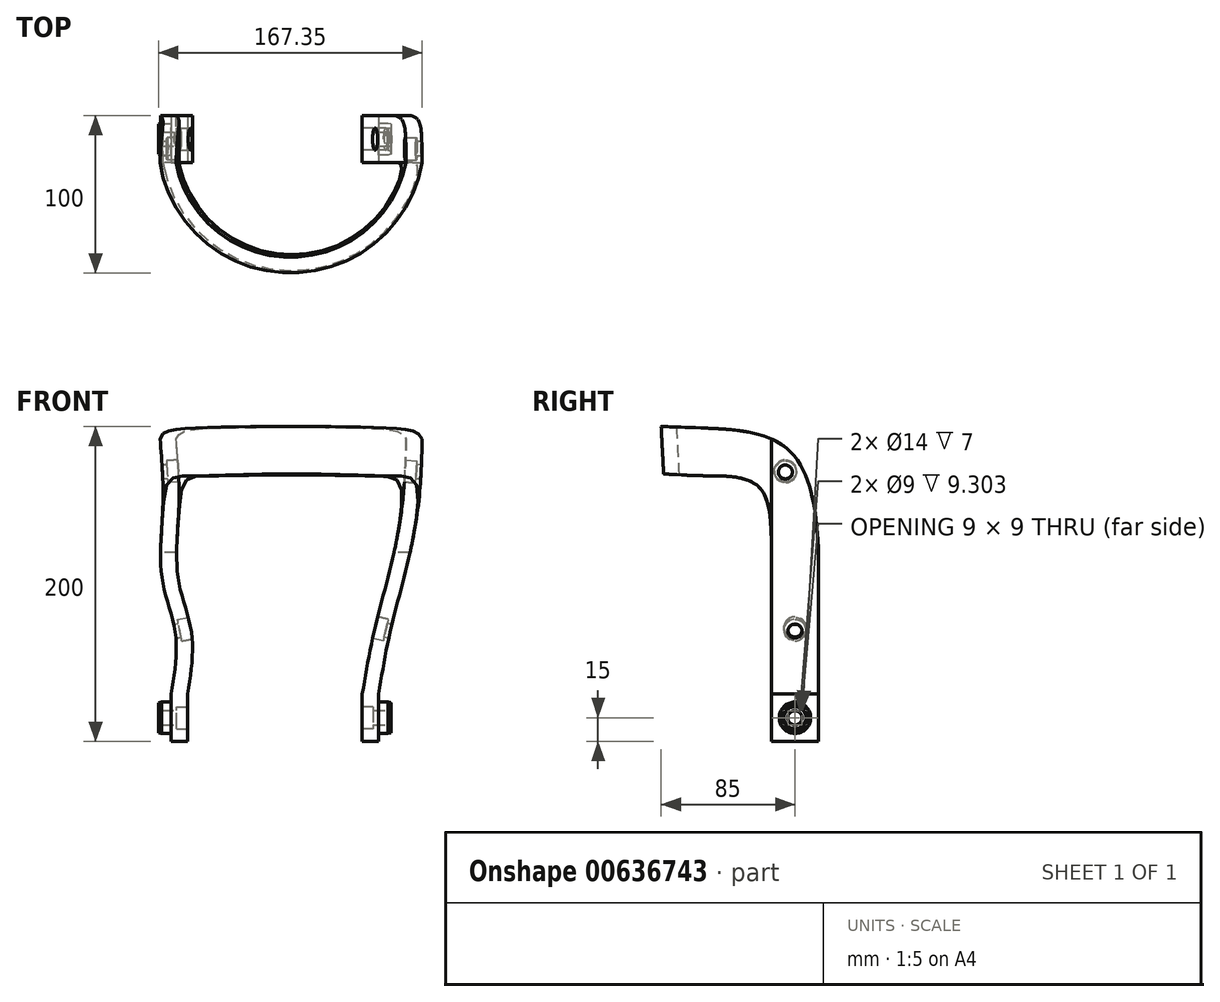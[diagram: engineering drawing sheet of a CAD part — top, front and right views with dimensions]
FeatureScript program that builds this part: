
annotation { "Feature Type Name" : "Feature", "Feature Type Description" : "" }
export const myFeature = defineFeature(function(context is Context, id is Id, definition is map)
    precondition{}
    {
        {
            var Q0;
            Q0=qCreatedBy(makeId("Top.planeOp"),FACE);
            var sketch = newSketch(context, id + "F0", { "sketchPlane" : qUnion([Q0])});
            skLineSegment(sketch, "E0", {"start": v(-55.5, 15) * mm, "end": v(-55.5, -15) * mm});
            skLineSegment(sketch, "E1", {"start": v(55.5, 15) * mm, "end": v(55.5, -15) * mm});
            skPoint(sketch, "E2", {"position": v(-55.5, 0) * mm});
            skPoint(sketch, "E3", {"position": v(55.5, 0) * mm});
            skLineSegment(sketch, "E4", {"start": v(-55.5, 15) * mm, "end": v(-65.81, 15) * mm});
            skLineSegment(sketch, "E5", {"start": v(-65.81, 15) * mm, "end": v(-65.81, -15) * mm});
            skLineSegment(sketch, "E6", {"start": v(55.5, 15) * mm, "end": v(65.81, 15) * mm});
            skLineSegment(sketch, "E7", {"start": v(65.81, 15) * mm, "end": v(65.81, -15) * mm});
            skLineSegment(sketch, "E8", {"start": v(-65.81, -15) * mm, "end": v(-55.5, -15) * mm});
            skLineSegment(sketch, "E9", {"start": v(55.5, -15) * mm, "end": v(65.81, -15) * mm});
            skSolve(sketch);
        }
        {
            var Q0;
            Q0=qCreatedBy(makeId("Top.planeOp"),FACE);
            cPlane(context, id + "F1", {"entities" : qUnion([Q0]), "cplaneType" : CPlaneType.OFFSET, "offset" : 30 * mm, "width" : 150 * mm, "height" : 150 * mm});
        }
        {
            var Q0;
            Q0=qCreatedBy(id+"F1.planeOp",FACE);
            var sketch = newSketch(context, id + "F2", { "sketchPlane" : qUnion([Q0])});
            skArc(sketch, "E10", {"start": v(-55.5, -15) * mm, "mid": v(0, -57.5) * mm, "end": v(55.5, -15) * mm});
            skArc(sketch, "E11", {"start": v(-65.81, -15) * mm, "mid": v(0, -67.5) * mm, "end": v(65.81, -15) * mm});
            skLineSegment(sketch, "E12", {"start": v(-55.5, 15) * mm, "end": v(-55.5, -15) * mm});
            skLineSegment(sketch, "E13", {"start": v(55.5, 15) * mm, "end": v(55.5, -15) * mm});
            skPoint(sketch, "E14", {"position": v(-55.5, 0) * mm});
            skPoint(sketch, "E15", {"position": v(55.5, 0) * mm});
            skLineSegment(sketch, "E16", {"start": v(-55.5, 15) * mm, "end": v(-65.81, 15) * mm});
            skLineSegment(sketch, "E17", {"start": v(-65.81, 15) * mm, "end": v(-65.81, -15) * mm});
            skLineSegment(sketch, "E18", {"start": v(55.5, 15) * mm, "end": v(65.81, 15) * mm});
            skLineSegment(sketch, "E19", {"start": v(65.81, 15) * mm, "end": v(65.81, -15) * mm});
            skSolve(sketch);
        }
        {
            var Q0;
            Q0=qCreatedBy(makeId("Top.planeOp"),FACE);
            cPlane(context, id + "F3", {"entities" : qUnion([Q0]), "cplaneType" : CPlaneType.OFFSET, "offset" : 70 * mm, "width" : 150 * mm, "height" : 150 * mm});
        }
        {
            var Q0;
            Q0=qCreatedBy(id+"F3.planeOp",FACE);
            var sketch = newSketch(context, id + "F4", { "sketchPlane" : qUnion([Q0])});
            skPoint(sketch, "E20", {"position": v(5, 0) * mm});
            skPoint(sketch, "E21.center.orphan", {"position": v(0, 0) * mm});
            skArc(sketch, "E22", {"start": v(-53.1, -15) * mm, "mid": v(5, -60) * mm, "end": v(63.1, -15) * mm});
            skArc(sketch, "E23", {"start": v(-63.37, -15) * mm, "mid": v(5, -70) * mm, "end": v(73.37, -15) * mm});
            skLineSegment(sketch, "E24", {"start": v(-53.1, 15) * mm, "end": v(-53.1, -15) * mm});
            skLineSegment(sketch, "E25", {"start": v(63.1, 15) * mm, "end": v(63.1, -15) * mm});
            skPoint(sketch, "E26", {"position": v(-53.1, 0) * mm});
            skLineSegment(sketch, "E27", {"start": v(-53.1, 15) * mm, "end": v(-63.37, 15) * mm});
            skLineSegment(sketch, "E28", {"start": v(-63.37, 15) * mm, "end": v(-63.37, -15) * mm});
            skLineSegment(sketch, "E29", {"start": v(63.1, 15) * mm, "end": v(73.37, 15) * mm});
            skLineSegment(sketch, "E30", {"start": v(73.37, 15) * mm, "end": v(73.37, -15) * mm});
            skSolve(sketch);
        }
        {
            var Q0;
            Q0=qCreatedBy(makeId("Top.planeOp"),FACE);
            cPlane(context, id + "F5", {"entities" : qUnion([Q0]), "cplaneType" : CPlaneType.OFFSET, "offset" : 100 * mm, "width" : 150 * mm, "height" : 150 * mm});
        }
        {
            var Q0;
            Q0=qCreatedBy(id+"F5.planeOp",FACE);
            var sketch = newSketch(context, id + "F6", { "sketchPlane" : qUnion([Q0])});
            skPoint(sketch, "E31", {"position": v(5, 0) * mm});
            skArc(sketch, "E32", {"start": v(-60.81, -15) * mm, "mid": v(5, -67.5) * mm, "end": v(70.81, -15) * mm});
            skArc(sketch, "E33", {"start": v(-71.03, -15) * mm, "mid": v(5, -77.5) * mm, "end": v(81.03, -15) * mm});
            skLineSegment(sketch, "E34", {"start": v(-60.81, 15) * mm, "end": v(-60.81, -15) * mm});
            skLineSegment(sketch, "E35", {"start": v(70.81, 15) * mm, "end": v(70.81, -15) * mm});
            skLineSegment(sketch, "E36", {"start": v(-60.81, 15) * mm, "end": v(-71.03, 15) * mm});
            skLineSegment(sketch, "E37", {"start": v(-71.03, 15) * mm, "end": v(-71.03, -15) * mm});
            skLineSegment(sketch, "E38", {"start": v(70.81, 15) * mm, "end": v(81.03, 15) * mm});
            skLineSegment(sketch, "E39", {"start": v(81.03, 15) * mm, "end": v(81.03, -15) * mm});
            skSolve(sketch);
        }
        {
            var Q0;
            Q0=qCreatedBy(makeId("Top.planeOp"),FACE);
            cPlane(context, id + "F7", {"entities" : qUnion([Q0]), "cplaneType" : CPlaneType.OFFSET, "offset" : 150 * mm, "width" : 150 * mm, "height" : 150 * mm});
        }
        {
            var Q0;
            Q0=qCreatedBy(id+"F7.planeOp",FACE);
            var sketch = newSketch(context, id + "F8", { "sketchPlane" : qUnion([Q0])});
            skPoint(sketch, "E40", {"position": v(10, 0) * mm});
            skArc(sketch, "E41", {"start": v(-60.93, -15) * mm, "mid": v(10, -72.5) * mm, "end": v(80.93, -15) * mm});
            skArc(sketch, "E42", {"start": v(-71.12, -15) * mm, "mid": v(10, -82.5) * mm, "end": v(91.12, -15) * mm});
            skLineSegment(sketch, "E43", {"start": v(-60.93, 15) * mm, "end": v(-60.93, -15) * mm});
            skLineSegment(sketch, "E44", {"start": v(80.93, -15) * mm, "end": v(80.93, 15) * mm});
            skPoint(sketch, "E45", {"position": v(-60.93, 0) * mm});
            skPoint(sketch, "E46", {"position": v(80.93, 0) * mm});
            skLineSegment(sketch, "E47", {"start": v(-60.93, 15) * mm, "end": v(-71.12, 15) * mm});
            skLineSegment(sketch, "E48", {"start": v(-71.12, 15) * mm, "end": v(-71.12, -15) * mm});
            skLineSegment(sketch, "E49", {"start": v(80.93, 15) * mm, "end": v(91.12, 15) * mm});
            skLineSegment(sketch, "E50", {"start": v(91.12, 15) * mm, "end": v(91.12, -15) * mm});
            skSolve(sketch);
        }
        {
            var Q0;
            Q0=qCreatedBy(makeId("Top.planeOp"),FACE);
            cPlane(context, id + "F9", {"entities" : qUnion([Q0]), "cplaneType" : CPlaneType.OFFSET, "offset" : 200 * mm, "width" : 150 * mm, "height" : 150 * mm});
        }
        {
            var Q0;
            Q0=qCreatedBy(id+"F9.planeOp",FACE);
            var sketch = newSketch(context, id + "F10", { "sketchPlane" : qUnion([Q0])});
            skPoint(sketch, "E51", {"position": v(10, 0) * mm});
            skArc(sketch, "E52", {"start": v(-63.48, -15) * mm, "mid": v(10, -75) * mm, "end": v(83.48, -15) * mm});
            skArc(sketch, "E53", {"start": v(-73.67, -15) * mm, "mid": v(10, -85) * mm, "end": v(93.67, -15) * mm});
            skLineSegment(sketch, "E54", {"start": v(-63.48, 15) * mm, "end": v(-63.48, -15) * mm});
            skLineSegment(sketch, "E55", {"start": v(83.48, 15) * mm, "end": v(83.48, -15) * mm});
            skLineSegment(sketch, "E56", {"start": v(-63.48, 15) * mm, "end": v(-73.67, 15) * mm});
            skLineSegment(sketch, "E57", {"start": v(-73.67, 15) * mm, "end": v(-73.67, -15) * mm});
            skLineSegment(sketch, "E58", {"start": v(83.48, 15) * mm, "end": v(93.67, 15) * mm});
            skLineSegment(sketch, "E59", {"start": v(93.67, 15) * mm, "end": v(93.67, -15) * mm});
            skSolve(sketch);
        }
        {
            var Q0;
            Q0=qSketchRegion(id+"F2",true);
            var Q1;
            Q1=qSketchRegion(id+"F4",true);
            var Q2;
            Q2=qSketchRegion(id+"F6",true);
            var Q3;
            Q3=qSketchRegion(id+"F8",true);
            var Q4;
            Q4=qSketchRegion(id+"F10",true);
            loft(context, id + "F11", {"sheetProfilesArray" : [{ "sheetProfileEntities" : qUnion([Q0]) }, { "sheetProfileEntities" : qUnion([Q1]) }, { "sheetProfileEntities" : qUnion([Q2]) }, { "sheetProfileEntities" : qUnion([Q3]) }, { "sheetProfileEntities" : qUnion([Q4]) }]});
        }
        {
            var Q0;
            Q0=qCreatedBy(makeId("Right.planeOp"),FACE);
            cPlane(context, id + "F12", {"entities" : qUnion([Q0]), "cplaneType" : CPlaneType.OFFSET, "offset" : 77 * mm, "oppositeDirection" : true, "width" : 150 * mm, "height" : 150 * mm});
        }
        {
            var Q0;
            Q0=qCreatedBy(id+"F12.planeOp",FACE);
            var sketch = newSketch(context, id + "F13", { "sketchPlane" : qUnion([Q0])});
            skPoint(sketch, "E60", {"position": v(-85, 200) * mm});
            skLineSegment(sketch, "E61", {"start": v(-85, 200) * mm, "end": v(-85, 170) * mm});
            skPoint(sketch, "E62", {"position": v(15, 200) * mm});
            skLineSegment(sketch, "E63", {"start": v(15, 200) * mm, "end": v(15, 120) * mm});
            skPoint(sketch, "E64", {"position": v(15, 0) * mm});
            skPoint(sketch, "E65", {"position": v(-15, 0) * mm});
            skPoint(sketch, "E66", {"position": v(-15, 200) * mm});
            skFitSpline(sketch, "E67", {"points": [v(-85, 200) * mm, v(15, 120) * mm], "startDerivative": vector(199.24, -8.69) * mm, "endDerivative": vector(9.95, -251.27) * mm});
            skPoint(sketch, "E68", {"position": v(-56.51, 168.7) * mm});
            skPoint(sketch, "E69", {"position": v(-23.21, 161.98) * mm});
            skPoint(sketch, "E70", {"position": v(-50.86, 198.7) * mm});
            skPoint(sketch, "E71", {"position": v(-4.39, 185.34) * mm});
            skPoint(sketch, "E72", {"position": v(-15, 120) * mm});
            skFitSpline(sketch, "E73", {"points": [v(-15, 120) * mm, v(-23.21, 161.98) * mm, v(-56.51, 168.7) * mm, v(-85, 170) * mm], "startDerivative": vector(0.5, 138.75) * mm, "endDerivative": vector(-88.02, 5.85) * mm});
            skLineSegment(sketch, "E74", {"start": v(-15, 120) * mm, "end": v(-15, 0) * mm});
            skLineSegment(sketch, "E75", {"start": v(15, 0) * mm, "end": v(15, 120) * mm});
            skLineSegment(sketch, "E76", {"start": v(-85, 200) * mm, "end": v(15, 200) * mm});
            skLineSegment(sketch, "E77", {"start": v(-85, 170) * mm, "end": v(-82.46, 0) * mm});
            skLineSegment(sketch, "E78", {"start": v(-82.46, 0) * mm, "end": v(-15, 0) * mm});
            skLineSegment(sketch, "E79", {"start": v(-85, 170) * mm, "end": v(-85, 200) * mm});
            skSolve(sketch);
        }
        {
            var Q0;
            Q0=qSketchRegion(id+"F13",true);
            extrude(context, id + "F14", {"entities" : qUnion([Q0]), "operationType" : NewBodyOperationType.REMOVE, "depth" : 300 * mm, "offsetDistance" : 25 * mm});
        }
        {
            var Q0;
            Q0=qCreatedBy(id+"F12.planeOp",FACE);
            var sketch = newSketch(context, id + "F15", { "sketchPlane" : qUnion([Q0])});
            skPoint(sketch, "E80", {"position": v(-8.62, 171.05) * mm});
            skLineSegment(sketch, "E81.bottom", {"start": v(-11.12, 161.05) * mm, "end": v(-6.12, 161.05) * mm});
            skLineSegment(sketch, "E81.top", {"start": v(-11.12, 181.05) * mm, "end": v(-6.12, 181.05) * mm});
            skLineSegment(sketch, "E81.left", {"start": v(-11.12, 161.05) * mm, "end": v(-11.12, 181.05) * mm});
            skLineSegment(sketch, "E81.right", {"start": v(-6.12, 161.05) * mm, "end": v(-6.12, 181.05) * mm});
            skSolve(sketch);
        }
        {
            var Q0;
            Q0=qSketchRegion(id+"F0",true);
            extrude(context, id + "F16", {"entities" : qUnion([Q0]), "operationType" : NewBodyOperationType.ADD, "depth" : 30 * mm, "offsetDistance" : 25 * mm});
        }
        {
            var Q0;
            Q0=makeQuery(id+"F16.opExtrude","SWEPT_FACE",FACE,{"disambiguationData":[OSD([sQuery(id+"F0.wireOp",EDGE,"E7")])]});
            var sketch = newSketch(context, id + "F17", { "sketchPlane" : qUnion([Q0])});
            skPoint(sketch, "E82", {"position": v(-15, 30) * mm});
            skPoint(sketch, "E83", {"position": v(-15, 0) * mm});
            skPoint(sketch, "E84", {"position": v(0, 15) * mm});
            skCircle(sketch, "E85", {"center": v(0, 15) * mm, "radius": 10 * mm});
            skSolve(sketch);
        }
        {
            var Q0;
            Q0=qSketchRegion(id+"F17",true);
            extrude(context, id + "F18", {"entities" : qUnion([Q0]), "operationType" : NewBodyOperationType.ADD, "depth" : 6 * mm, "offsetDistance" : 25 * mm});
        }
        {
            var Q0;
            Q0=makeQuery(id+"F18.opExtrude","CAP_FACE",FACE,{"disambiguationData":[OSD([sQuery(id+"F17.wireOp",EDGE,"E85")])],"isStart":false});
            cPlane(context, id + "F19", {"entities" : qUnion([Q0]), "cplaneType" : CPlaneType.OFFSET, "offset" : 0 * mm, "width" : 150 * mm, "height" : 150 * mm});
        }
        {
            var Q0;
            Q0=makeQuery(id+"F16.opExtrude","SWEPT_FACE",FACE,{"disambiguationData":[OSD([sQuery(id+"F0.wireOp",EDGE,"E1")])]});
            cPlane(context, id + "F20", {"entities" : qUnion([Q0]), "cplaneType" : CPlaneType.OFFSET, "offset" : 0 * mm, "width" : 150 * mm, "height" : 150 * mm});
        }
        {
            var Q0;
            Q0=qCreatedBy(id+"F20.planeOp",FACE);
            var sketch = newSketch(context, id + "F21", { "sketchPlane" : qUnion([Q0])});
            skPoint(sketch, "E86", {"position": v(0, 0) * mm});
            skPoint(sketch, "E87", {"position": v(0, 15) * mm});
            skCircle(sketch, "E88", {"center": v(0, 15) * mm, "radius": 7 * mm});
            skSolve(sketch);
        }
        {
            var Q0;
            Q0=qSketchRegion(id+"F21",true);
            extrude(context, id + "F22", {"entities" : qUnion([Q0]), "operationType" : NewBodyOperationType.REMOVE, "oppositeDirection" : true, "depth" : 7 * mm, "offsetDistance" : 25 * mm});
        }
        {
            var Q0;
            Q0=makeQuery(id+"F16.opExtrude","SWEPT_FACE",FACE,{"disambiguationData":[OSD([sQuery(id+"F0.wireOp",EDGE,"E5")])]});
            cPlane(context, id + "F23", {"entities" : qUnion([Q0]), "cplaneType" : CPlaneType.OFFSET, "offset" : 0 * mm, "width" : 150 * mm, "height" : 150 * mm});
        }
        {
            var Q0;
            Q0=qCreatedBy(id+"F23.planeOp",FACE);
            var sketch = newSketch(context, id + "F24", { "sketchPlane" : qUnion([Q0])});
            skPoint(sketch, "E89", {"position": v(0, 15) * mm});
            skCircle(sketch, "E90", {"center": v(0, 15) * mm, "radius": 10 * mm});
            skSolve(sketch);
        }
        {
            var Q0;
            Q0=qSketchRegion(id+"F24",true);
            extrude(context, id + "F25", {"entities" : qUnion([Q0]), "operationType" : NewBodyOperationType.ADD, "depth" : 6 * mm, "offsetDistance" : 25 * mm});
        }
        {
            var Q0;
            Q0=makeQuery(id+"F25.opExtrude","CAP_FACE",FACE,{"disambiguationData":[OSD([sQuery(id+"F24.wireOp",EDGE,"E90")])],"isStart":false});
            cPlane(context, id + "F26", {"entities" : qUnion([Q0]), "cplaneType" : CPlaneType.OFFSET, "offset" : 0 * mm, "width" : 150 * mm, "height" : 150 * mm});
        }
        {
            var Q0;
            Q0=makeQuery(id+"F16.opExtrude","SWEPT_FACE",FACE,{"disambiguationData":[OSD([sQuery(id+"F0.wireOp",EDGE,"E0")])]});
            cPlane(context, id + "F27", {"entities" : qUnion([Q0]), "cplaneType" : CPlaneType.OFFSET, "offset" : 0 * mm, "width" : 150 * mm, "height" : 150 * mm});
        }
        {
            var Q0;
            Q0=qCreatedBy(id+"F27.planeOp",FACE);
            var sketch = newSketch(context, id + "F28", { "sketchPlane" : qUnion([Q0])});
            skPoint(sketch, "E91", {"position": v(0, 0) * mm});
            skPoint(sketch, "E92", {"position": v(0, 15) * mm});
            skCircle(sketch, "E93", {"center": v(0, 15) * mm, "radius": 7 * mm});
            skSolve(sketch);
        }
        {
            var Q0;
            Q0=qSketchRegion(id+"F28",true);
            extrude(context, id + "F29", {"entities" : qUnion([Q0]), "operationType" : NewBodyOperationType.REMOVE, "oppositeDirection" : true, "depth" : 7 * mm, "offsetDistance" : 25 * mm});
        }
        {
            var Q0;
            Q0=makeQuery(id+"F16.opExtrude","CAP_FACE",FACE,{"disambiguationData":[OSD([sQuery(id+"F0.wireOp",EDGE,"E1"),sQuery(id+"F0.wireOp",EDGE,"E6"),sQuery(id+"F0.wireOp",EDGE,"E7"),sQuery(id+"F0.wireOp",EDGE,"E9")])],"isStart":true});
            cPlane(context, id + "F30", {"entities" : qUnion([Q0]), "cplaneType" : CPlaneType.OFFSET, "offset" : 15 * mm, "oppositeDirection" : true, "width" : 150 * mm, "height" : 150 * mm});
        }
        {
            var Q0;
            Q0=qCreatedBy(id+"F30.planeOp",FACE);
            var sketch = newSketch(context, id + "F31", { "sketchPlane" : qUnion([Q0])});
            skPoint(sketch, "E94", {"position": v(60.66, -15) * mm});
            skLineSegment(sketch, "E95", {"start": v(60.66, -15) * mm, "end": v(61.72, -15) * mm, "construction": true});
            skPoint(sketch, "E96", {"position": v(71.81, 4.05) * mm});
            skPoint(sketch, "E97", {"position": v(71.81, -12) * mm});
            skPoint(sketch, "E98", {"position": v(71.81, -15) * mm});
            skPoint(sketch, "E99", {"position": v(41.37, 7.31) * mm});
            skPoint(sketch, "E100", {"position": v(71.81, -13.5) * mm});
            skPoint(sketch, "E101", {"position": v(73.81, -13.5) * mm});
            skPoint(sketch, "E102", {"position": v(73.81, -12.5) * mm});
            skPoint(sketch, "E103", {"position": v(73.81, -14.5) * mm});
            skLineSegment(sketch, "E104", {"start": v(71.81, -12) * mm, "end": v(71.81, -15) * mm});
            skPoint(sketch, "E105", {"position": v(71.81, 0) * mm});
            skPoint(sketch, "E106", {"position": v(71.81, -10) * mm});
            skPoint(sketch, "E107", {"position": v(65.81, -10) * mm});
            skPoint(sketch, "E108", {"position": v(65.81, -7) * mm});
            skPoint(sketch, "E109", {"position": v(65.81, -8.5) * mm});
            skPoint(sketch, "E110", {"position": v(67.81, -8.5) * mm});
            skPoint(sketch, "E111", {"position": v(67.81, -7.5) * mm});
            skPoint(sketch, "E112", {"position": v(67.81, -9.5) * mm});
            skPoint(sketch, "E113", {"position": v(65.81, 0) * mm});
            skLineSegment(sketch, "E114.trimOffspring", {"start": v(71.81, -10) * mm, "end": v(71.81, -16.41) * mm, "construction": true});
            skPoint(sketch, "E115", {"position": v(71.81, -7) * mm});
            skPoint(sketch, "E116", {"position": v(71.81, -8.5) * mm});
            skPoint(sketch, "E117", {"position": v(73.81, -8.5) * mm});
            skPoint(sketch, "E118", {"position": v(73.81, -7.5) * mm});
            skPoint(sketch, "E119", {"position": v(73.81, -9.5) * mm});
            skLineSegment(sketch, "E120", {"start": v(73.81, -7.5) * mm, "end": v(71.81, -7) * mm});
            skLineSegment(sketch, "E121", {"start": v(73.81, -9.5) * mm, "end": v(73.81, -7.5) * mm});
            skLineSegment(sketch, "E122", {"start": v(73.81, -9.5) * mm, "end": v(71.81, -10) * mm});
            skLineSegment(sketch, "E123", {"start": v(71.81, -7) * mm, "end": v(71.81, -10) * mm});
            skLineSegment(sketch, "E124", {"start": v(71.81, 0) * mm, "end": v(73.81, 0) * mm});
            skLineSegment(sketch, "E125", {"start": v(73.81, -8.5) * mm, "end": v(73.81, -9.5) * mm});
            skSolve(sketch);
        }
        {
            var Q0;
            Q0=qSketchRegion(id+"F31",true);
            var Q1;
            Q1=sQuery(id+"F31.wireOp",EDGE,"E124");
            revolve(context, id + "F32", {"operationType" : NewBodyOperationType.ADD, "entities" : qUnion([Q0]), "axis" : qUnion([Q1]), "revolveType" : RevolveType.FULL});
        }
        {
            var Q0;
            Q0=qCreatedBy(id+"F19.planeOp",FACE);
            var sketch = newSketch(context, id + "F33", { "sketchPlane" : qUnion([Q0])});
            skPoint(sketch, "E126", {"position": v(0, 15) * mm});
            skPoint(sketch, "E127", {"position": v(0, 0) * mm});
            skCircle(sketch, "E128", {"center": v(0, 15) * mm, "radius": 4.5 * mm});
            skSolve(sketch);
        }
        {
            var Q0;
            Q0=qSketchRegion(id+"F33",true);
            extrude(context, id + "F34", {"entities" : qUnion([Q0]), "operationType" : NewBodyOperationType.REMOVE, "oppositeDirection" : true, "depth" : 25 * mm, "offsetDistance" : 25 * mm});
        }
        {
            var Q0;
            Q0=makeQuery(id+"F16.opExtrude","CAP_FACE",FACE,{"disambiguationData":[OSD([sQuery(id+"F0.wireOp",EDGE,"E0"),sQuery(id+"F0.wireOp",EDGE,"E4"),sQuery(id+"F0.wireOp",EDGE,"E5"),sQuery(id+"F0.wireOp",EDGE,"E8")])],"isStart":true});
            cPlane(context, id + "F35", {"entities" : qUnion([Q0]), "cplaneType" : CPlaneType.OFFSET, "offset" : 15 * mm, "oppositeDirection" : true, "width" : 150 * mm, "height" : 150 * mm});
        }
        {
            var Q0;
            Q0=qCreatedBy(id+"F35.planeOp",FACE);
            var sketch = newSketch(context, id + "F36", { "sketchPlane" : qUnion([Q0])});
            skPoint(sketch, "E129", {"position": v(-60.91, -32.93) * mm});
            skPoint(sketch, "E130", {"position": v(-65.81, -10) * mm});
            skPoint(sketch, "E131", {"position": v(-57.6, -34.18) * mm});
            skPoint(sketch, "E132", {"position": v(-65.81, -15) * mm});
            skPoint(sketch, "E133", {"position": v(-71.81, -10) * mm});
            skPoint(sketch, "E134", {"position": v(-71.81, -7) * mm});
            skPoint(sketch, "E135", {"position": v(-71.81, -8.5) * mm});
            skPoint(sketch, "E136", {"position": v(-73.81, -8.5) * mm});
            skPoint(sketch, "E137", {"position": v(-73.81, -9.5) * mm});
            skPoint(sketch, "E138", {"position": v(-73.81, -7.5) * mm});
            skLineSegment(sketch, "E139", {"start": v(-73.81, -9.5) * mm, "end": v(-71.81, -10) * mm});
            skLineSegment(sketch, "E140", {"start": v(-73.81, -7.5) * mm, "end": v(-73.81, -9.5) * mm});
            skLineSegment(sketch, "E141", {"start": v(-73.81, -7.5) * mm, "end": v(-71.81, -7) * mm});
            skLineSegment(sketch, "E142", {"start": v(-71.81, -10) * mm, "end": v(-71.81, -7) * mm});
            skLineSegment(sketch, "E143", {"start": v(-73.81, -8.5) * mm, "end": v(-73.81, -7.5) * mm});
            skSolve(sketch);
        }
        {
            var Q0;
            Q0=qCreatedBy(id+"F35.planeOp",FACE);
            var sketch = newSketch(context, id + "F37", { "sketchPlane" : qUnion([Q0])});
            skPoint(sketch, "E144", {"position": v(-71.81, -10) * mm});
            skPoint(sketch, "E145", {"position": v(-71.81, 0) * mm});
            skLineSegment(sketch, "E146", {"start": v(-71.81, 0) * mm, "end": v(-73.81, 0) * mm});
            skSolve(sketch);
        }
        {
            var Q0;
            Q0=qSketchRegion(id+"F36",true);
            var Q1;
            Q1=sQuery(id+"F37.wireOp",EDGE,"E146");
            revolve(context, id + "F38", {"operationType" : NewBodyOperationType.ADD, "entities" : qUnion([Q0]), "axis" : qUnion([Q1]), "revolveType" : RevolveType.FULL});
        }
        {
            var Q0;
            Q0=qCreatedBy(id+"F27.planeOp",FACE);
            var sketch = newSketch(context, id + "F39", { "sketchPlane" : qUnion([Q0])});
            skPoint(sketch, "E147", {"position": v(0, 0) * mm});
            skPoint(sketch, "E148", {"position": v(0, 15) * mm});
            skCircle(sketch, "E149", {"center": v(0, 15) * mm, "radius": 4.5 * mm});
            skSolve(sketch);
        }
        {
            var Q0;
            Q0=qSketchRegion(id+"F39",true);
            extrude(context, id + "F40", {"entities" : qUnion([Q0]), "operationType" : NewBodyOperationType.REMOVE, "oppositeDirection" : true, "depth" : 25 * mm, "offsetDistance" : 25 * mm});
        }
        {
            var Q0;
            Q0=qCreatedBy(makeId("Front.planeOp"),FACE);
            var sketch = newSketch(context, id + "F41", { "sketchPlane" : qUnion([Q0])});
            skPoint(sketch, "E150", {"position": v(73.37, 70) * mm});
            skLineSegment(sketch, "E151", {"start": v(73.37, 70) * mm, "end": v(63.46, 72.38) * mm});
            skPoint(sketch, "E152", {"position": v(75.25, 77.79) * mm});
            skLineSegment(sketch, "E153", {"start": v(75.25, 77.79) * mm, "end": v(73.37, 70) * mm});
            skLineSegment(sketch, "E154", {"start": v(73.37, 70) * mm, "end": v(61.05, 70) * mm});
            skLineSegment(sketch, "E155", {"start": v(75.25, 77.79) * mm, "end": v(75.25, 67.22) * mm});
            skLineSegment(sketch, "E156", {"start": v(73.37, 70) * mm, "end": v(84.33, 70) * mm});
            skPoint(sketch, "E157", {"position": v(0, 86.32) * mm});
            skPoint(sketch, "E158", {"position": v(0, 70) * mm});
            skLineSegment(sketch, "E159", {"start": v(73.37, 70) * mm, "end": v(73.37, 43.45) * mm});
            skLineSegment(sketch, "E160", {"start": v(73.37, 43.45) * mm, "end": v(73.37, 82.09) * mm});
            skSolve(sketch);
        }
        {
            var Q0;
            Q0=qCreatedBy(makeId("Right.planeOp"),FACE);
            cPlane(context, id + "F42", {"entities" : qUnion([Q0]), "cplaneType" : CPlaneType.OFFSET, "offset" : 73.37 * mm, "width" : 150 * mm, "height" : 150 * mm});
        }
        {
            var Q0;
            Q0=qCreatedBy(id+"F42.planeOp",FACE);
            var sketch = newSketch(context, id + "F43", { "sketchPlane" : qUnion([Q0])});
            skPoint(sketch, "E161", {"position": v(0, 70) * mm});
            skLineSegment(sketch, "E162", {"start": v(0, 70) * mm, "end": v(42.97, 70) * mm});
            skLineSegment(sketch, "E163", {"start": v(42.97, 70) * mm, "end": v(-53.34, 70) * mm});
            skSolve(sketch);
        }
        {
            var Q0;
            Q0=sQuery(id+"F43.wireOp",EDGE,"E163");
            var Q1;
            Q1=qCreatedBy(id+"F3.planeOp",FACE);
            cPlane(context, id + "F44", {"entities" : qUnion([Q0, Q1]), "cplaneType" : CPlaneType.LINE_ANGLE, "offset" : 25 * mm, "angle" : 103.53 * degree, "oppositeDirection" : true, "width" : 150 * mm, "height" : 150 * mm});
        }
        {
            var Q0;
            Q0=qCreatedBy(id+"F44.planeOp",FACE);
            var sketch = newSketch(context, id + "F45", { "sketchPlane" : qUnion([Q0])});
            skPoint(sketch, "E164", {"position": v(-7.5, 50.04) * mm});
            skPoint(sketch, "E165", {"position": v(0, 85.22) * mm});
            skCircle(sketch, "E166", {"center": v(0, 85.22) * mm, "radius": 4.5 * mm});
            skSolve(sketch);
        }
        {
            var Q0;
            Q0=qSketchRegion(id+"F45",true);
            extrude(context, id + "F46", {"entities" : qUnion([Q0]), "operationType" : NewBodyOperationType.REMOVE, "depth" : 50 * mm, "offsetDistance" : 25 * mm});
        }
        {
            var Q0;
            Q0=qSketchRegion(id+"F45",true);
            extrude(context, id + "F47", {"entities" : qUnion([Q0]), "operationType" : NewBodyOperationType.REMOVE, "oppositeDirection" : true, "depth" : 25 * mm, "offsetDistance" : 25 * mm});
        }
        {
            var Q0;
            Q0=qCreatedBy(id+"F44.planeOp",FACE);
            cPlane(context, id + "F48", {"entities" : qUnion([Q0]), "cplaneType" : CPlaneType.OFFSET, "offset" : 10 * mm, "width" : 150 * mm, "height" : 150 * mm});
        }
        {
            var Q0;
            Q0=qCreatedBy(id+"F48.planeOp",FACE);
            var sketch = newSketch(context, id + "F49", { "sketchPlane" : qUnion([Q0])});
            skPoint(sketch, "E167", {"position": v(0, 85.22) * mm});
            skCircle(sketch, "E168", {"center": v(0, 85.22) * mm, "radius": 7 * mm});
            skSolve(sketch);
        }
        {
            var Q0;
            Q0=qSketchRegion(id+"F49",true);
            extrude(context, id + "F50", {"entities" : qUnion([Q0]), "operationType" : NewBodyOperationType.REMOVE, "oppositeDirection" : true, "depth" : 7 * mm, "offsetDistance" : 25 * mm});
        }
        {
            var Q0;
            Q0=qSketchRegion(id+"F49",true);
            extrude(context, id + "F51", {"entities" : qUnion([Q0]), "operationType" : NewBodyOperationType.REMOVE, "depth" : 25 * mm, "offsetDistance" : 25 * mm});
        }
        {
            var Q0;
            Q0=qCreatedBy(makeId("Front.planeOp"),FACE);
            var sketch = newSketch(context, id + "F52", { "sketchPlane" : qUnion([Q0])});
            skPoint(sketch, "E169", {"position": v(-63.37, 70) * mm});
            skLineSegment(sketch, "E170", {"start": v(-63.37, 70) * mm, "end": v(-50.4, 70) * mm});
            skLineSegment(sketch, "E171", {"start": v(-50.4, 70) * mm, "end": v(-73.13, 70) * mm});
            skLineSegment(sketch, "E172", {"start": v(-63.37, 70) * mm, "end": v(-63.37, 75.73) * mm});
            skLineSegment(sketch, "E173", {"start": v(-63.37, 75.73) * mm, "end": v(-63.37, 61.67) * mm});
            skPoint(sketch, "E174", {"position": v(-64.51, 75.7) * mm});
            skLineSegment(sketch, "E175", {"start": v(-64.51, 75.7) * mm, "end": v(-63.37, 70) * mm});
            skSolve(sketch);
        }
        {
            var Q0;
            Q0=qCreatedBy(makeId("Right.planeOp"),FACE);
            cPlane(context, id + "F53", {"entities" : qUnion([Q0]), "cplaneType" : CPlaneType.OFFSET, "offset" : 63.37 * mm, "oppositeDirection" : true, "width" : 150 * mm, "height" : 150 * mm});
        }
        {
            var Q0;
            Q0=qCreatedBy(id+"F53.planeOp",FACE);
            var sketch = newSketch(context, id + "F54", { "sketchPlane" : qUnion([Q0])});
            skPoint(sketch, "E176", {"position": v(0, 70) * mm});
            skLineSegment(sketch, "E177", {"start": v(0, 70) * mm, "end": v(25.43, 70) * mm});
            skLineSegment(sketch, "E178", {"start": v(25.43, 70) * mm, "end": v(-27.36, 70) * mm});
            skSolve(sketch);
        }
        {
            var Q0;
            Q0=sQuery(id+"F54.wireOp",EDGE,"E178");
            var Q1;
            Q1=qCreatedBy(id+"F3.planeOp",FACE);
            cPlane(context, id + "F55", {"entities" : qUnion([Q0, Q1]), "cplaneType" : CPlaneType.LINE_ANGLE, "offset" : 25 * mm, "angle" : 101.3 * degree, "width" : 150 * mm, "height" : 150 * mm});
        }
        {
            var Q0;
            Q0=qCreatedBy(id+"F55.planeOp",FACE);
            var sketch = newSketch(context, id + "F56", { "sketchPlane" : qUnion([Q0])});
            skPoint(sketch, "E179", {"position": v(-3.92, 95.47) * mm});
            skPoint(sketch, "E180", {"position": v(0, 81.05) * mm});
            skCircle(sketch, "E181", {"center": v(0, 81.05) * mm, "radius": 4.5 * mm});
            skSolve(sketch);
        }
        {
            var Q0;
            Q0=qSketchRegion(id+"F56",true);
            extrude(context, id + "F57", {"entities" : qUnion([Q0]), "operationType" : NewBodyOperationType.REMOVE, "oppositeDirection" : true, "depth" : 25 * mm, "offsetDistance" : 25 * mm});
        }
        {
            var Q0;
            Q0=qSketchRegion(id+"F56",true);
            extrude(context, id + "F58", {"entities" : qUnion([Q0]), "operationType" : NewBodyOperationType.REMOVE, "depth" : 25 * mm, "offsetDistance" : 25 * mm});
        }
        {
            var Q0;
            Q0=qCreatedBy(id+"F55.planeOp",FACE);
            cPlane(context, id + "F59", {"entities" : qUnion([Q0]), "cplaneType" : CPlaneType.OFFSET, "offset" : 10 * mm, "width" : 150 * mm, "height" : 150 * mm});
        }
        {
            var Q0;
            Q0=qCreatedBy(id+"F59.planeOp",FACE);
            var sketch = newSketch(context, id + "F60", { "sketchPlane" : qUnion([Q0])});
            skPoint(sketch, "E182", {"position": v(0, 81.05) * mm});
            skCircle(sketch, "E183", {"center": v(0, 81.05) * mm, "radius": 7 * mm});
            skSolve(sketch);
        }
        {
            var Q0;
            Q0=qSketchRegion(id+"F60",true);
            extrude(context, id + "F61", {"entities" : qUnion([Q0]), "operationType" : NewBodyOperationType.REMOVE, "oppositeDirection" : true, "depth" : 7 * mm, "offsetDistance" : 25 * mm});
        }
        {
            var Q0;
            Q0=qSketchRegion(id+"F60",true);
            extrude(context, id + "F62", {"entities" : qUnion([Q0]), "operationType" : NewBodyOperationType.REMOVE, "depth" : 25 * mm, "offsetDistance" : 25 * mm});
        }
        {
            var Q0;
            Q0=qCreatedBy(makeId("Front.planeOp"),FACE);
            var sketch = newSketch(context, id + "F63", { "sketchPlane" : qUnion([Q0])});
            skPoint(sketch, "E184", {"position": v(-71.4, 171.06) * mm});
            skPoint(sketch, "E185", {"position": v(92.88, 171.04) * mm});
            skLineSegment(sketch, "E186", {"start": v(-71.4, 171.06) * mm, "end": v(-71.4, 188.4) * mm});
            skLineSegment(sketch, "E187", {"start": v(-71.4, 188.4) * mm, "end": v(-71.4, 150.8) * mm});
            skLineSegment(sketch, "E188", {"start": v(-71.4, 171.06) * mm, "end": v(-97.97, 171.06) * mm});
            skPoint(sketch, "E189", {"position": v(-72.56, 187.66) * mm});
            skLineSegment(sketch, "E190", {"start": v(-72.56, 187.66) * mm, "end": v(-71.4, 171.06) * mm});
            skSolve(sketch);
        }
        {
            var Q0;
            Q0=qCreatedBy(makeId("Right.planeOp"),FACE);
            cPlane(context, id + "F64", {"entities" : qUnion([Q0]), "cplaneType" : CPlaneType.OFFSET, "offset" : 92.88 * mm, "width" : 150 * mm, "height" : 150 * mm});
        }
        {
            var Q0;
            Q0=qCreatedBy(id+"F64.planeOp",FACE);
            var sketch = newSketch(context, id + "F65", { "sketchPlane" : qUnion([Q0])});
            skPoint(sketch, "E191", {"position": v(-6.12, 171.06) * mm});
            skLineSegment(sketch, "E192", {"start": v(-6.12, 171.06) * mm, "end": v(-23.57, 171.06) * mm});
            skLineSegment(sketch, "E193", {"start": v(-23.57, 171.06) * mm, "end": v(12.77, 171.06) * mm});
            skSolve(sketch);
        }
        {
            var Q0;
            Q0=qCreatedBy(makeId("Front.planeOp"),FACE);
            var sketch = newSketch(context, id + "F66", { "sketchPlane" : qUnion([Q0])});
            skPoint(sketch, "E194", {"position": v(92.88, 171.06) * mm});
            skPoint(sketch, "E195", {"position": v(0, 0) * mm});
            skSolve(sketch);
        }
        {
            var Q0;
            Q0=qCreatedBy(makeId("Top.planeOp"),FACE);
            cPlane(context, id + "F67", {"entities" : qUnion([Q0]), "cplaneType" : CPlaneType.OFFSET, "offset" : 171.06 * mm, "width" : 150 * mm, "height" : 150 * mm});
        }
        {
            var Q0;
            Q0=sQuery(id+"F65.wireOp",EDGE,"E193");
            var Q1;
            Q1=qCreatedBy(id+"F67.planeOp",FACE);
            cPlane(context, id + "F68", {"entities" : qUnion([Q0, Q1]), "cplaneType" : CPlaneType.LINE_ANGLE, "offset" : 25 * mm, "angle" : 86.15 * degree, "oppositeDirection" : true, "width" : 150 * mm, "height" : 150 * mm});
        }
        {
            var Q0;
            Q0=qCreatedBy(id+"F68.planeOp",FACE);
            var sketch = newSketch(context, id + "F69", { "sketchPlane" : qUnion([Q0])});
            skPoint(sketch, "E196", {"position": v(-6.12, 176.9) * mm});
            skCircle(sketch, "E197", {"center": v(-6.12, 176.9) * mm, "radius": 4.5 * mm});
            skSolve(sketch);
        }
        {
            var Q0;
            Q0=qSketchRegion(id+"F69",true);
            extrude(context, id + "F70", {"entities" : qUnion([Q0]), "operationType" : NewBodyOperationType.REMOVE, "depth" : 25 * mm, "offsetDistance" : 25 * mm});
        }
        {
            var Q0;
            Q0=qSketchRegion(id+"F69",true);
            extrude(context, id + "F71", {"entities" : qUnion([Q0]), "operationType" : NewBodyOperationType.REMOVE, "oppositeDirection" : true, "depth" : 25 * mm, "offsetDistance" : 25 * mm});
        }
        {
            var Q0;
            Q0=qCreatedBy(makeId("Right.planeOp"),FACE);
            cPlane(context, id + "F72", {"entities" : qUnion([Q0]), "cplaneType" : CPlaneType.OFFSET, "offset" : 71.4 * mm, "oppositeDirection" : true, "width" : 150 * mm, "height" : 150 * mm});
        }
        {
            var Q0;
            Q0=qCreatedBy(id+"F72.planeOp",FACE);
            var sketch = newSketch(context, id + "F73", { "sketchPlane" : qUnion([Q0])});
            skPoint(sketch, "E198", {"position": v(-240.56, 249.3) * mm});
            skPoint(sketch, "E199", {"position": v(-6.12, 171.06) * mm});
            skLineSegment(sketch, "E200", {"start": v(-6.12, 171.06) * mm, "end": v(-30.39, 171.06) * mm});
            skSolve(sketch);
        }
        {
            var Q0;
            Q0=sQuery(id+"F73.wireOp",EDGE,"E200");
            var Q1;
            Q1=qCreatedBy(id+"F67.planeOp",FACE);
            cPlane(context, id + "F74", {"entities" : qUnion([Q0, Q1]), "cplaneType" : CPlaneType.LINE_ANGLE, "offset" : 25 * mm, "angle" : 86.02 * degree, "oppositeDirection" : true, "width" : 150 * mm, "height" : 150 * mm});
        }
        {
            var Q0;
            Q0=qCreatedBy(id+"F74.planeOp",FACE);
            var sketch = newSketch(context, id + "F75", { "sketchPlane" : qUnion([Q0])});
            skPoint(sketch, "E201", {"position": v(6.12, 175.6) * mm});
            skCircle(sketch, "E202", {"center": v(6.12, 175.6) * mm, "radius": 4.5 * mm});
            skSolve(sketch);
        }
        {
            var Q0;
            Q0=qSketchRegion(id+"F75",true);
            extrude(context, id + "F76", {"entities" : qUnion([Q0]), "operationType" : NewBodyOperationType.REMOVE, "oppositeDirection" : true, "depth" : 25 * mm, "offsetDistance" : 25 * mm});
        }
        {
            var Q0;
            Q0=qSketchRegion(id+"F75",true);
            extrude(context, id + "F77", {"entities" : qUnion([Q0]), "operationType" : NewBodyOperationType.REMOVE, "depth" : 25 * mm, "offsetDistance" : 25 * mm});
        }
        {
            var Q0;
            Q0=qCreatedBy(id+"F74.planeOp",FACE);
            cPlane(context, id + "F78", {"entities" : qUnion([Q0]), "cplaneType" : CPlaneType.OFFSET, "offset" : 10 * mm, "oppositeDirection" : true, "width" : 150 * mm, "height" : 150 * mm});
        }
        {
            var Q0;
            Q0=qCreatedBy(id+"F78.planeOp",FACE);
            var sketch = newSketch(context, id + "F79", { "sketchPlane" : qUnion([Q0])});
            skPoint(sketch, "E203", {"position": v(6.12, 175.6) * mm});
            skCircle(sketch, "E204", {"center": v(6.12, 175.6) * mm, "radius": 7 * mm});
            skSolve(sketch);
        }
        {
            var Q0;
            Q0=qSketchRegion(id+"F79",true);
            extrude(context, id + "F80", {"entities" : qUnion([Q0]), "operationType" : NewBodyOperationType.REMOVE, "oppositeDirection" : true, "depth" : 7 * mm, "offsetDistance" : 25 * mm});
        }
        {
            var Q0;
            Q0=qSketchRegion(id+"F79",true);
            extrude(context, id + "F81", {"entities" : qUnion([Q0]), "operationType" : NewBodyOperationType.REMOVE, "depth" : 7 * mm, "offsetDistance" : 25 * mm});
        }
        {
            var Q0;
            Q0=qCreatedBy(id+"F68.planeOp",FACE);
            cPlane(context, id + "F82", {"entities" : qUnion([Q0]), "cplaneType" : CPlaneType.OFFSET, "offset" : 10 * mm, "oppositeDirection" : true, "width" : 150 * mm, "height" : 150 * mm});
        }
        {
            var Q0;
            Q0=qCreatedBy(id+"F82.planeOp",FACE);
            var sketch = newSketch(context, id + "F83", { "sketchPlane" : qUnion([Q0])});
            skPoint(sketch, "E205", {"position": v(-6.12, 176.9) * mm});
            skCircle(sketch, "E206", {"center": v(-6.12, 176.9) * mm, "radius": 7 * mm});
            skSolve(sketch);
        }
        {
            var Q0;
            Q0=qSketchRegion(id+"F83",true);
            extrude(context, id + "F84", {"entities" : qUnion([Q0]), "operationType" : NewBodyOperationType.REMOVE, "oppositeDirection" : true, "depth" : 7 * mm, "offsetDistance" : 25 * mm});
        }
        {
            var Q0;
            Q0=qSketchRegion(id+"F83",true);
            extrude(context, id + "F85", {"entities" : qUnion([Q0]), "operationType" : NewBodyOperationType.REMOVE, "depth" : 7 * mm, "offsetDistance" : 25 * mm});
        }
    });
